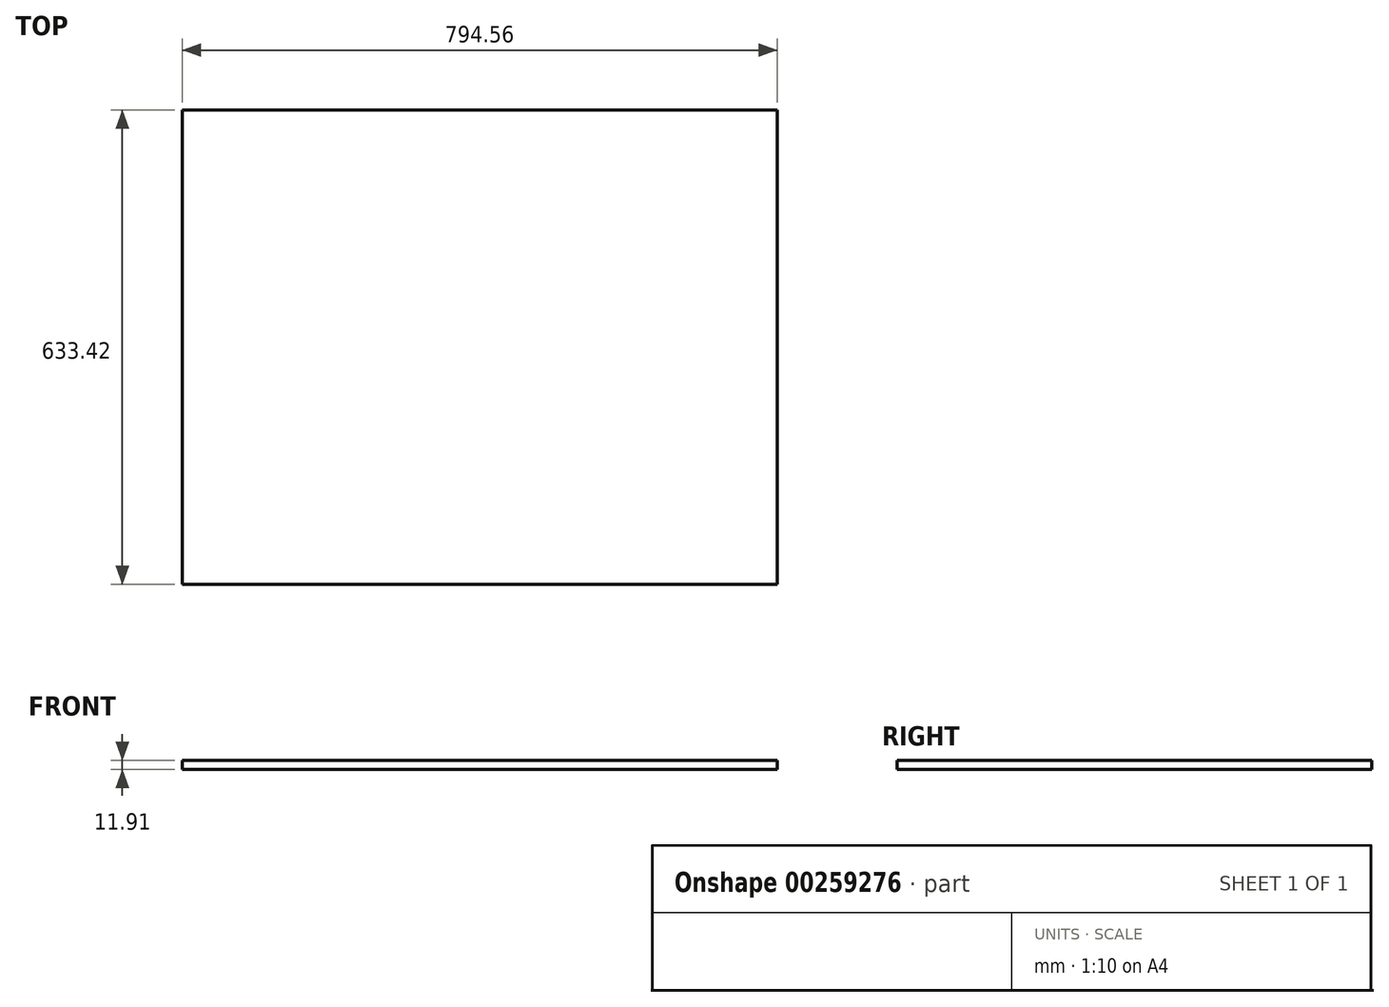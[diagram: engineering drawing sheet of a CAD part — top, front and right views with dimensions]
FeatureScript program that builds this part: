
annotation { "Feature Type Name" : "Feature", "Feature Type Description" : "" }
export const myFeature = defineFeature(function(context is Context, id is Id, definition is map)
    precondition{}
    {
        {
            var Q0;
            Q0=qCreatedBy(makeId("Top.planeOp"),FACE);
            var sketch = newSketch(context, id + "F0", { "sketchPlane" : qUnion([Q0])});
            skLineSegment(sketch, "E0.bottom", {"start": v(-397.28, 316.7) * mm, "end": v(397.28, 316.7) * mm});
            skLineSegment(sketch, "E0.top", {"start": v(-397.28, -316.7) * mm, "end": v(397.28, -316.7) * mm});
            skLineSegment(sketch, "E0.left", {"start": v(-397.28, 316.7) * mm, "end": v(-397.28, -316.7) * mm});
            skLineSegment(sketch, "E0.right", {"start": v(397.28, 316.7) * mm, "end": v(397.28, -316.7) * mm});
            skPoint(sketch, "E0.middle", {"position": v(0, 0) * mm});
            skSolve(sketch);
        }
        {
            var Q0;
            Q0=makeQuery(id+"F0.imprint","IMPRINT",FACE,{"disambiguationData":[TD([[makeQuery(id+"F0.imprint","IMPRINT",EDGE,{"derivedFrom":sQuery(id+"F0.wireOp",EDGE,"E0.bottom")}),-1.0]])]});
            extrude(context, id + "F1", {"entities" : qUnion([Q0]), "depth" : 11.9 * mm});
        }
    });
